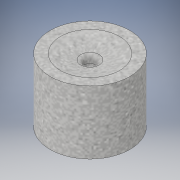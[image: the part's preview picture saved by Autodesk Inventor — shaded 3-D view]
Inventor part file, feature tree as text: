
AUTODESK INVENTOR PART (.ipt)
format: ipt  version: 2017 (Build 210142000, 142)  size: 158,208 bytes
history: native  units: in
note: dims shown in document units (in); Inventor stores cm internally (conversion verified against a paired STEP export)
features: revolve x1, sketch x1
ambient origin geometry x8: Origin, YZ Plane, XZ Plane, XY Plane, X Axis, Y Axis, Z Axis, Center Point
bodies: Solid1 (feature_tree)
feature tree (2):
  revolve  "Revolution1"  [1 undecoded]
  sketch  "Sketch1"  dims[d0=0.25in d1=0.1718in d2=15.0deg d4=0.25in d5=1.5in d6=1.25in d7=0.25in d11=0.25in d13=0.5in d15=0.25in d16=0.25in d18=0.125in d19=0.5in d20=0.125in d21=0.25in d22=0.125in d23=0.125in d24=0.25in d25=0.5in d26=2.292in d27=0.5in d28=90.0deg]
note: 1 required parameter value undecoded (feature->parameter linkage not recoverable at this tier; creation-order binding heuristic only, values carry confidence <= 0.55)
